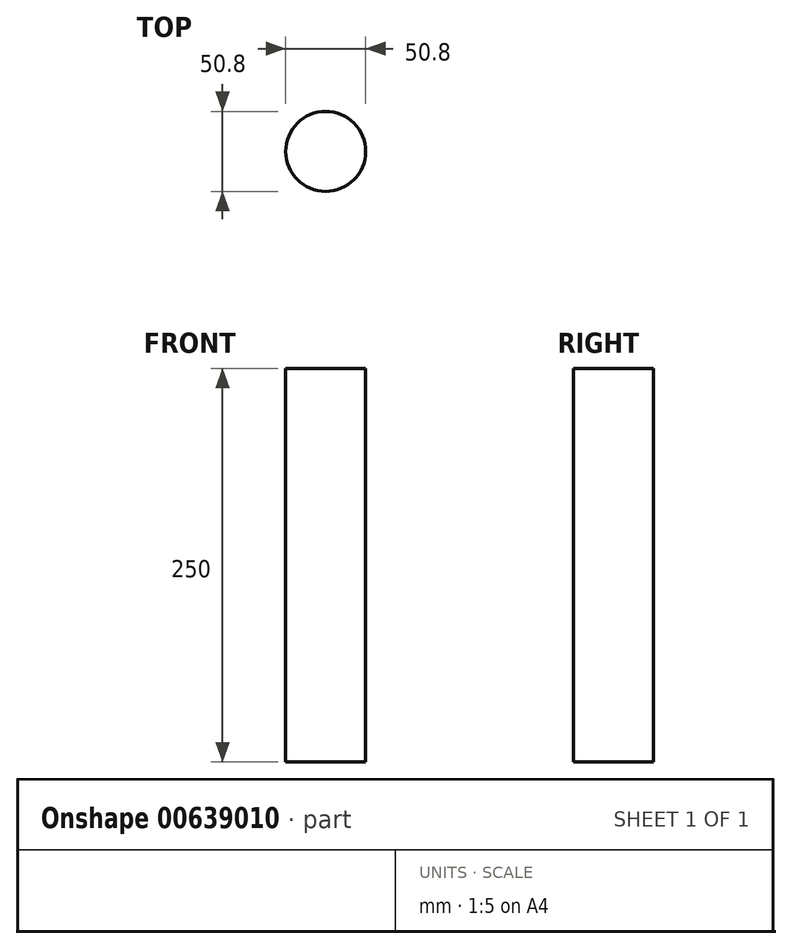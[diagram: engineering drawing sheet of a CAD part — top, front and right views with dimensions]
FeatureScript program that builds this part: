
annotation { "Feature Type Name" : "Feature", "Feature Type Description" : "" }
export const myFeature = defineFeature(function(context is Context, id is Id, definition is map)
    precondition{}
    {
        {
            var Q0;
            Q0=qCreatedBy(makeId("Top.planeOp"),FACE);
            var sketch = newSketch(context, id + "F0", { "sketchPlane" : qUnion([Q0])});
            skCircle(sketch, "E0", {"center": v(0, 0) * mm, "radius": 25.4 * mm});
            skSolve(sketch);
        }
        {
            var Q0;
            Q0=makeQuery(id+"F0.imprint","IMPRINT",FACE,{"disambiguationData":[TD([[makeQuery(id+"F0.imprint","IMPRINT",EDGE,{"derivedFrom":sQuery(id+"F0.wireOp",EDGE,"E0")}),1.0]])]});
            extrude(context, id + "F1", {"entities" : qUnion([Q0]), "depth" : 250 * mm, "offsetDistance" : 25 * mm});
        }
    });
